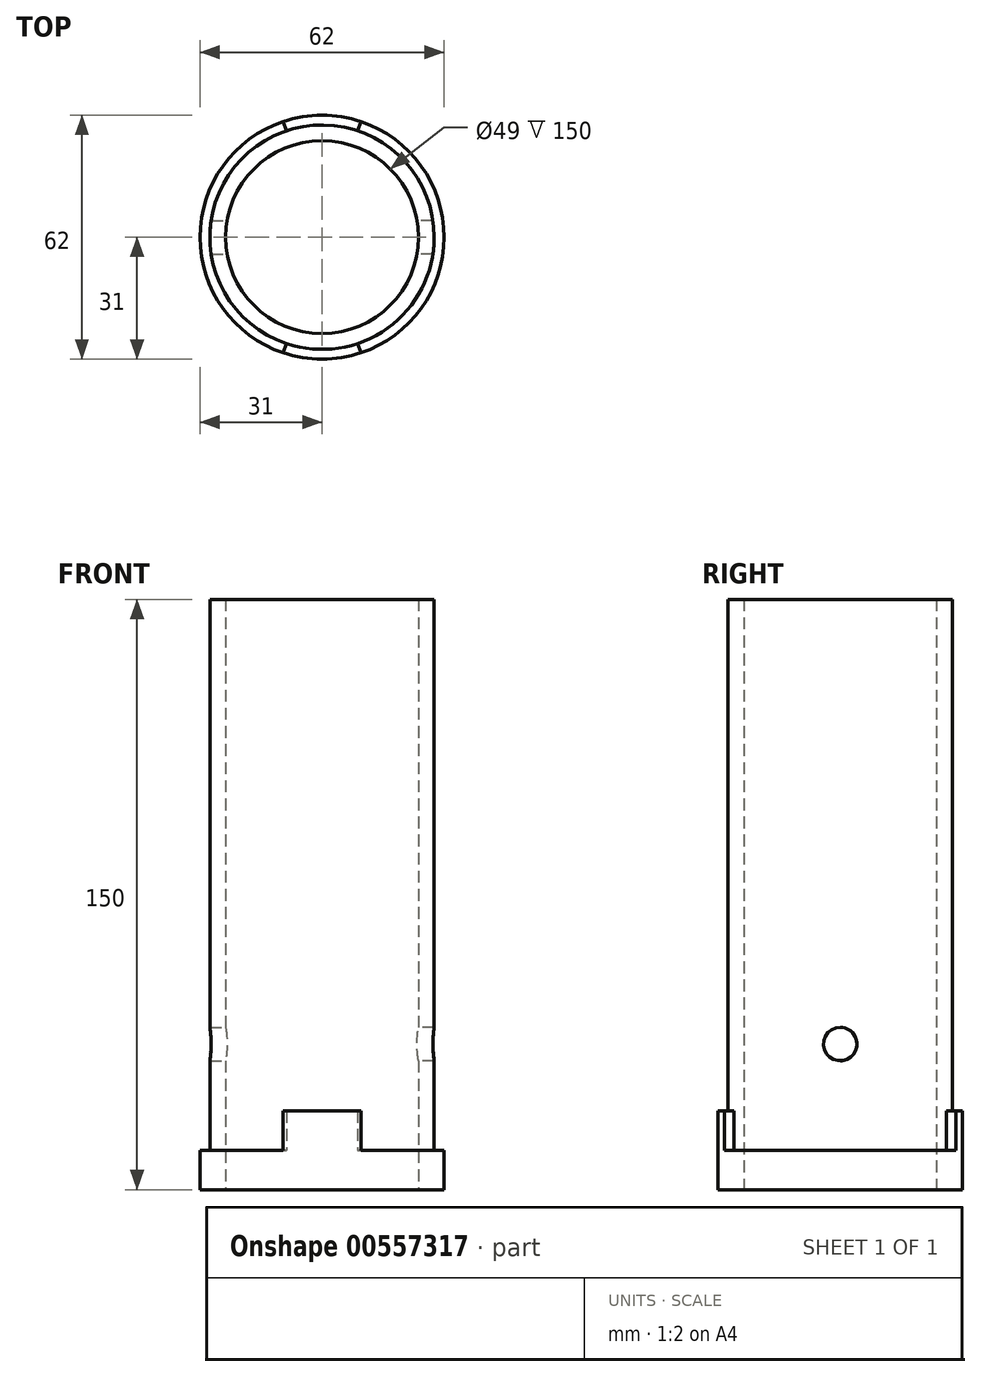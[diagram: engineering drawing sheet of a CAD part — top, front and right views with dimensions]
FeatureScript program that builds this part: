
annotation { "Feature Type Name" : "Feature", "Feature Type Description" : "" }
export const myFeature = defineFeature(function(context is Context, id is Id, definition is map)
    precondition{}
    {
        {
            var Q0;
            Q0=qCreatedBy(makeId("Top.planeOp"),FACE);
            var sketch = newSketch(context, id + "F0", { "sketchPlane" : qUnion([Q0])});
            skCircle(sketch, "E0", {"center": v(0, 0) * mm, "radius": 28.5 * mm});
            skCircle(sketch, "E1", {"center": v(0, 0) * mm, "radius": 24.5 * mm});
            skCircle(sketch, "E2", {"center": v(0, 0) * mm, "radius": 31 * mm});
            skLineSegment(sketch, "E3", {"start": v(9.87, 29.39) * mm, "end": v(9.07, 27.02) * mm});
            skLineSegment(sketch, "E4.MirrorCS", {"start": v(-9.87, 29.39) * mm, "end": v(-9.07, 27.02) * mm});
            skLineSegment(sketch, "E5.left", {"start": v(-9.07, 27.02) * mm, "end": v(-9.07, 27.02) * mm});
            skLineSegment(sketch, "E5.right", {"start": v(9.07, 27.02) * mm, "end": v(9.07, 27.02) * mm});
            skLineSegment(sketch, "E6.left", {"start": v(-9.87, 29.39) * mm, "end": v(-9.87, 29.39) * mm});
            skLineSegment(sketch, "E6.right", {"start": v(9.87, 29.39) * mm, "end": v(9.87, 29.39) * mm});
            skLineSegment(sketch, "E7", {"start": v(-9.07, -27.02) * mm, "end": v(-9.87, -29.39) * mm});
            skLineSegment(sketch, "E8", {"start": v(9.07, -27.02) * mm, "end": v(9.87, -29.39) * mm});
            skSolve(sketch);
        }
        {
            var Q0;
            Q0=makeQuery(id+"F0.imprint","IMPRINT",FACE,{"disambiguationData":[TD([[makeQuery(id+"F0.imprint","IMPRINT",EDGE,{"derivedFrom":sQuery(id+"F0.wireOp",EDGE,"E0")}),-1.0]])]});
            extrude(context, id + "F1", {"entities" : qUnion([Q0]), "depth" : 10 * mm, "offsetDistance" : 25 * mm});
        }
        {
            var Q0;
            Q0=makeQuery(id+"F0.imprint","IMPRINT",FACE,{"disambiguationData":[TD([[makeQuery(id+"F0.imprint","IMPRINT",EDGE,{"derivedFrom":sQuery(id+"F0.wireOp",EDGE,"E0")}),1.0]])]});
            extrude(context, id + "F2", {"entities" : qUnion([Q0]), "operationType" : NewBodyOperationType.ADD, "depth" : 150 * mm, "offsetDistance" : 25 * mm});
        }
        {
            var Q0;
            Q0=qCreatedBy(makeId("Right.planeOp"),FACE);
            var sketch = newSketch(context, id + "F3", { "sketchPlane" : qUnion([Q0])});
            skCircle(sketch, "E9", {"center": v(0, 37) * mm, "radius": 4.25 * mm});
            skSolve(sketch);
        }
        {
            var Q0;
            Q0=sQuery(id+"F3.wireOp",VERTEX,"E9.center");
            var Q1;
            Q1=makeQuery(id+"F1.opExtrude","SWEPT_BODY",BODY,{"disambiguationData":[OSD([sQuery(id+"F0.wireOp",EDGE,"E0"),sQuery(id+"F0.wireOp",EDGE,"E2")])]});
            hole(context, id + "F4", {"style" : HoleStyle.SIMPLE, "endStyle" : HoleEndStyle.THROUGH, "holeDiameter" : 8.5 * mm, "isTappedThrough" : true, "tappedDepth" : 12 * mm, "tapClearance" : 3, "locations" : qUnion([Q0]), "scope" : qUnion([Q1])});
        }
        {
            var Q0;
            Q0=sQuery(id+"F3.wireOp",VERTEX,"E9.center");
            var Q1;
            Q1=makeQuery(id+"F1.opExtrude","SWEPT_BODY",BODY,{"disambiguationData":[OSD([sQuery(id+"F0.wireOp",EDGE,"E0"),sQuery(id+"F0.wireOp",EDGE,"E2")])]});
            hole(context, id + "F5", {"style" : HoleStyle.SIMPLE, "endStyle" : HoleEndStyle.THROUGH, "oppositeDirection" : true, "holeDiameter" : 8.5 * mm, "isTappedThrough" : true, "tappedDepth" : 12 * mm, "tapClearance" : 3, "locations" : qUnion([Q0]), "scope" : qUnion([Q1])});
        }
        {
            var Q0;
            {var subQ0=sQuery(id+"F0.wireOp",EDGE,"E3");Q0=makeQuery(id+"F0.imprint","IMPRINT",FACE,{"disambiguationData":[TD([[makeQuery(id+"F0.imprint","IMPRINT",EDGE,{"derivedFrom":subQ0}),-1.0]])]});}
            extrude(context, id + "F6", {"entities" : qUnion([Q0]), "operationType" : NewBodyOperationType.ADD, "depth" : 20 * mm, "offsetDistance" : 25 * mm});
        }
        {
            var Q0;
            {var subQ0=sQuery(id+"F0.wireOp",EDGE,"E7");Q0=makeQuery(id+"F0.imprint","IMPRINT",FACE,{"disambiguationData":[TD([[makeQuery(id+"F0.imprint","IMPRINT",EDGE,{"derivedFrom":subQ0}),1.0]])]});}
            extrude(context, id + "F7", {"entities" : qUnion([Q0]), "operationType" : NewBodyOperationType.ADD, "depth" : 20 * mm, "offsetDistance" : 25 * mm});
        }
    });
